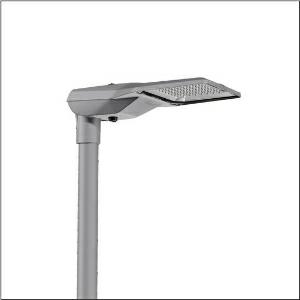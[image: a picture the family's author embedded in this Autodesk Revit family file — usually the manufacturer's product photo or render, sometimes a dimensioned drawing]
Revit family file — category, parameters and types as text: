
# Revit family: streetlight_sl_21_midi___st0_5a_5xe3b43t08nb_31ab
name_source: partatom
category: Lighting Fixtures
units: mm (PartAtom-declared; Revit-internal decimal feet)

## family parameters
Cut with Voids When Loaded = No
Host = Face
Light Source = No
Part Type = Normal
Room Calculation Point = No
Round Connector Dimension = Use Diameter
Shared = No

## types (1)
- --- (1 x LED, 23710 lm, 151.2 W, 4000K)
    Apparent Load = 151 VA
    CIE Flux Codes = 43 76 97 100 100
    Color Rendering = 70
    Color Temperature = 4000K
    Default Elevation = 1800 mm
    Description = Streetlight SL 21 midi, mast luminaire, primary light control with lens, of PMMA, primary optical cover: cover, of toughened safety glass, transparent, light distribution: ST0.5a, light emission: direct distribution, primary light characteristic: asymmetric, installation type: side-entry, post-top, LED, High Power LED, rated luminous flux: 23.710lm, luminous efficacy: 157lm/W, light colour: 740, colour temperature: 4000K, control gear: D4i, control: overheat protection, constant luminous flux control, time-dependent luminous flux control, flexible luminous flux parameterisation, pre-setting: logarithmic dimming characteristic, mains connection: 230..240V, AC, 50/60Hz, start of lifetime: 151W, end of service life: 157W, reduction: 70W, luminaire housing, of diecast aluminium, powder-coated, Siteco® metallic grey (DB 702S), corrosivity category C5 mid according to DIN EN ISO 12944, please order mast flange separately, inclination adjustable: 0°, 5°, 10°, 15°, sealing non-destructively replaceable, multi-level sealing system, length: 644mm, width: 335mm, height: 110mm, mast flange for spigot size: 42mm (side-entry): 5XC10008XM4, 60/48mm (side-entry/post-top): 5XC10108XM2, 76/60mm (side-entry/post-top): 5XC10108XM1, mounting height: 4..8m, Smart Interface below and above, protection rating (complete): IP66, insulation class (complete): insulation class II (safety insulation), certification: CE, ENEC, ENEC+, VDE, impact resistance: IK10, permissible operating ambient temperature for outdoor applications: -40..+50°C, standard-compliant lighting for roads and squares, packaging unit: 1 piece

Light Distribution: ST0.5a
    Height = 111 mm
    Lamp = 1 x LED
    Lamp Light Flux = 23710 lm
    Lamp Power = 151.2 W
    Lamp count = 1
    Length = 644 mm
    Luminous efficacy = 157 lm/W
    Manufacturer = Siteco
    ModVariant = No
    Model = 5XE3B43T08NB
    Number of Poles = 1
    OnlyDefault = Yes
    Power Factor = 1
    Product Name = Streetlight SL 21 midi | ST0.5a
    Product group = mast luminaire | pylon top
    ProductGroupID = 6100
    Protection Class = Protection class II
    Protection Degree = IP 66
    RLX_Detail_Level = 1
    RLX_Emergency_Light_Flux = 0 lm
    RLX_Emergency_Type = 0
    RLX_Emergency_Type_DB = No
    RlxData = <blob elided: 38257 chars, md5=32ddfa77>
    Socket = socket
    Standby Power = 0 W
    System Light Flux = 23710 lm
    System Power = 151 W
    Type Comments = factory setting: luminous flux: 100 % | dim-lin: 254 | 802 mA
    Type Image = l_1004304.jpg
    URL = http://relux.com
    VarID = @adj_192779
    Voltage = 0 V
    Weight = 0.00 kg
    Width = 336 mm

## geometry (parser evidence)
native form markers: Blend x4, Sweep x8
no freeform markers — native parametric forms only
